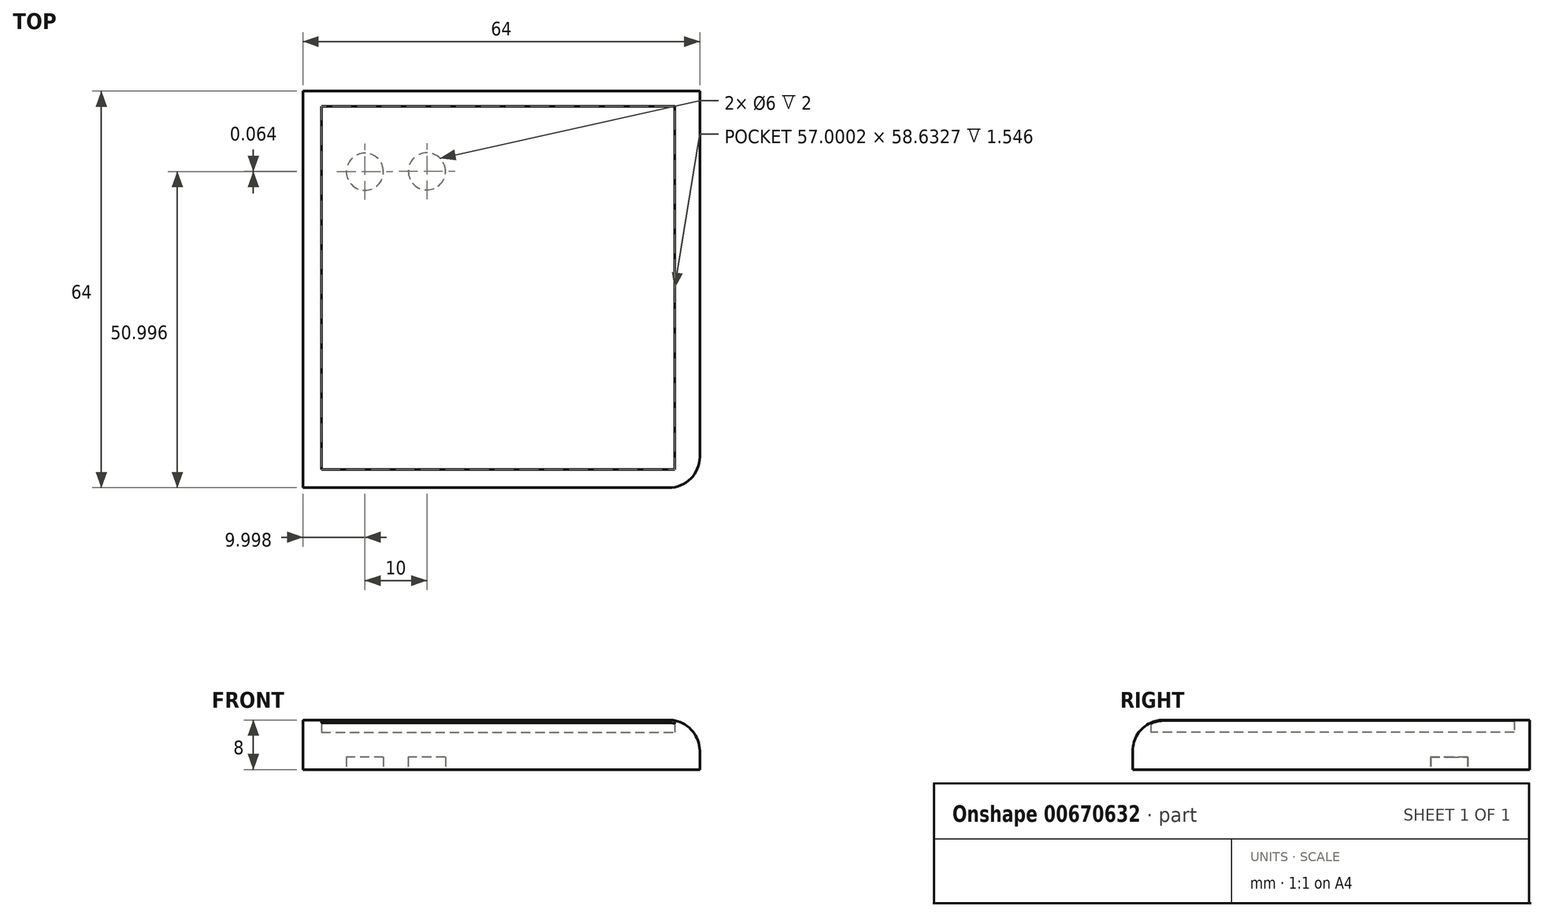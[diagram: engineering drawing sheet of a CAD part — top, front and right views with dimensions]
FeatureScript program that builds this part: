
annotation { "Feature Type Name" : "Feature", "Feature Type Description" : "" }
export const myFeature = defineFeature(function(context is Context, id is Id, definition is map)
    precondition{}
    {
        {
            var Q0;
            Q0=qCreatedBy(makeId("Top.planeOp"),FACE);
            var sketch = newSketch(context, id + "F0", { "sketchPlane" : qUnion([Q0])});
            skLineSegment(sketch, "E0.bottom", {"start": v(-26.1, 30.32) * mm, "end": v(37.9, 30.32) * mm});
            skLineSegment(sketch, "E0.top", {"start": v(-26.1, -33.68) * mm, "end": v(37.9, -33.68) * mm});
            skLineSegment(sketch, "E0.left", {"start": v(-26.1, 30.32) * mm, "end": v(-26.1, -33.68) * mm});
            skLineSegment(sketch, "E0.right", {"start": v(37.9, 30.32) * mm, "end": v(37.9, -33.68) * mm});
            skSolve(sketch);
        }
        {
            var Q0;
            Q0=makeQuery(id+"F0.imprint","IMPRINT",FACE,{"disambiguationData":[TD([[makeQuery(id+"F0.imprint","IMPRINT",EDGE,{"derivedFrom":sQuery(id+"F0.wireOp",EDGE,"E0.bottom")}),-1.0]])]});
            extrude(context, id + "F1", {"entities" : qUnion([Q0]), "depth" : 6 * mm, "offsetDistance" : 25 * mm});
        }
        {
            var Q0;
            Q0=qCreatedBy(makeId("Top.planeOp"),FACE);
            var sketch = newSketch(context, id + "F2", { "sketchPlane" : qUnion([Q0])});
            skCircle(sketch, "E1", {"center": v(-16.1, 17.32) * mm, "radius": 3 * mm});
            skCircle(sketch, "E2.1.0.0", {"center": v(-6.1, 17.38) * mm, "radius": 3 * mm});
            skCircle(sketch, "E2.2.0.0", {"center": v(3.9, 17.44) * mm, "radius": 3 * mm});
            skCircle(sketch, "E2.3.0.0", {"center": v(13.9, 17.5) * mm, "radius": 3 * mm});
            skCircle(sketch, "E2.4.0.0", {"center": v(23.9, 17.57) * mm, "radius": 3 * mm});
            skLineSegment(sketch, "E2.direction1", {"start": v(-16.1, 17.32) * mm, "end": v(-6.1, 17.38) * mm, "construction": true});
            skSolve(sketch);
        }
        {
            var Q0;
            Q0=makeQuery(id+"F2.imprint","IMPRINT",FACE,{"disambiguationData":[TD([[makeQuery(id+"F2.imprint","IMPRINT",EDGE,{"derivedFrom":sQuery(id+"F2.wireOp",EDGE,"E1")}),1.0]])]});
            var Q1;
            Q1=makeQuery(id+"F2.imprint","IMPRINT",FACE,{"disambiguationData":[TD([[makeQuery(id+"F2.imprint","IMPRINT",EDGE,{"derivedFrom":sQuery(id+"F2.wireOp",EDGE,"E2.1.0.0")}),1.0]])]});
            extrude(context, id + "F3", {"entities" : qUnion([Q0, Q1]), "operationType" : NewBodyOperationType.REMOVE, "depth" : 2 * mm, "offsetDistance" : 25 * mm});
        }
        {
            var Q0;
            Q0=makeQuery(id+"F1.opExtrude","CAP_FACE",FACE,{"disambiguationData":[OSD([sQuery(id+"F0.wireOp",EDGE,"E0.bottom"),sQuery(id+"F0.wireOp",EDGE,"E0.top"),sQuery(id+"F0.wireOp",EDGE,"E0.left"),sQuery(id+"F0.wireOp",EDGE,"E0.right")])],"isStart":false});
            var sketch = newSketch(context, id + "F4", { "sketchPlane" : qUnion([Q0])});
            skLineSegment(sketch, "E3", {"start": v(-26.1, 27.87) * mm, "end": v(37.9, 27.87) * mm});
            skLineSegment(sketch, "E4", {"start": v(-23.11, 27.87) * mm, "end": v(-23.11, -33.68) * mm});
            skLineSegment(sketch, "E5", {"start": v(-23.11, -30.77) * mm, "end": v(37.9, -30.77) * mm});
            skLineSegment(sketch, "E6", {"start": v(33.89, 27.87) * mm, "end": v(33.89, -30.77) * mm});
            skLineSegment(sketch, "E7", {"start": v(-26.1, 30.32) * mm, "end": v(37.9, 30.32) * mm});
            skLineSegment(sketch, "E8", {"start": v(37.9, 30.32) * mm, "end": v(37.9, -12.67) * mm});
            skLineSegment(sketch, "E9", {"start": v(37.9, -12.67) * mm, "end": v(37.9, -35.6) * mm});
            skLineSegment(sketch, "E10", {"start": v(37.9, -35.6) * mm, "end": v(-26.1, -35.6) * mm});
            skLineSegment(sketch, "E11", {"start": v(-26.1, -35.6) * mm, "end": v(-26.1, 30.32) * mm});
            skSolve(sketch);
        }
        {
            var Q0;
            {var subQ0=sQuery(id+"F4.wireOp",EDGE,"E11");var subQ3=sQuery(id+"F4.wireOp",EDGE,"E3");var subQ4=makeQuery(id+"F4.imprint","INTERSECT",VERTEX,{"derivedFrom":[subQ3,subQ0]});Q0=makeQuery(id+"F4.imprint","IMPRINT",FACE,{"disambiguationData":[TD([[makeQuery(id+"F4.imprint","IMPRINT",EDGE,{"disambiguationData":[TD([[subQ4,-1.0]])],"derivedFrom":subQ3}),-1.0]])]});}
            var Q1;
            {var subQ0=sQuery(id+"F4.wireOp",EDGE,"E7");Q1=makeQuery(id+"F4.imprint","IMPRINT",FACE,{"disambiguationData":[TD([[makeQuery(id+"F4.imprint","IMPRINT",EDGE,{"derivedFrom":subQ0}),-1.0]])]});}
            var Q2;
            {var subQ7=sQuery(id+"F4.wireOp",EDGE,"E6");Q2=makeQuery(id+"F4.imprint","IMPRINT",FACE,{"disambiguationData":[TD([[makeQuery(id+"F4.imprint","IMPRINT",EDGE,{"derivedFrom":subQ7}),1.0]])]});}
            var Q3;
            {var subQ1=makeQuery(id+"F1.opExtrude","CAP_EDGE",EDGE,{"disambiguationData":[OSD([sQuery(id+"F0.wireOp",EDGE,"E0.top")])],"isStart":false});var subQ6=sQuery(id+"F4.wireOp",EDGE,"E4");var subQ8=makeQuery(id+"F4.imprint","INTERSECT",VERTEX,{"derivedFrom":[subQ1,subQ6]});Q3=makeQuery(id+"F4.imprint","IMPRINT",FACE,{"disambiguationData":[TD([[makeQuery(id+"F4.imprint","IMPRINT",EDGE,{"disambiguationData":[TD([[subQ8,1.0]])],"derivedFrom":subQ6}),1.0]])]});}
            extrude(context, id + "F5", {"entities" : qUnion([Q0, Q1, Q2, Q3]), "operationType" : NewBodyOperationType.ADD, "depth" : 2 * mm, "offsetDistance" : 25 * mm});
        }
        {
            var Q0;
            Q0=makeQuery(id+"F5.opExtrude","CAP_EDGE",EDGE,{"disambiguationData":[OSD([sQuery(id+"F0.wireOp",EDGE,"E0.top")])],"isStart":false});
            var Q1;
            Q1=makeQuery(id+"F5.opExtrude","CAP_EDGE",EDGE,{"disambiguationData":[OSD([sQuery(id+"F4.wireOp",EDGE,"E8"),sQuery(id+"F4.wireOp",EDGE,"E9")])],"isStart":false});
            fillet(context, id + "F6", {"entities" : qUnion([Q0, Q1]), "radius" : 5 * mm, "tangentPropagation" : true, "allowEdgeOverflow" : false});
        }
        {
            var Q0;
            Q0=makeQuery(id+"F6.opFillet","BLEND_EDGE",EDGE,{"blendedFrom":[makeQuery(id+"F5.opExtrude","CAP_EDGE",EDGE,{"disambiguationData":[OSD([sQuery(id+"F4.wireOp",EDGE,"E8"),sQuery(id+"F4.wireOp",EDGE,"E9")])],"isStart":false}),makeQuery(id+"F5.opExtrude","CAP_EDGE",EDGE,{"disambiguationData":[OSD([sQuery(id+"F0.wireOp",EDGE,"E0.top")])],"isStart":false})],"blendedInto":[]});
            fillet(context, id + "F7", {"entities" : qUnion([Q0]), "radius" : 5 * mm, "tangentPropagation" : true, "allowEdgeOverflow" : false});
        }
    });
